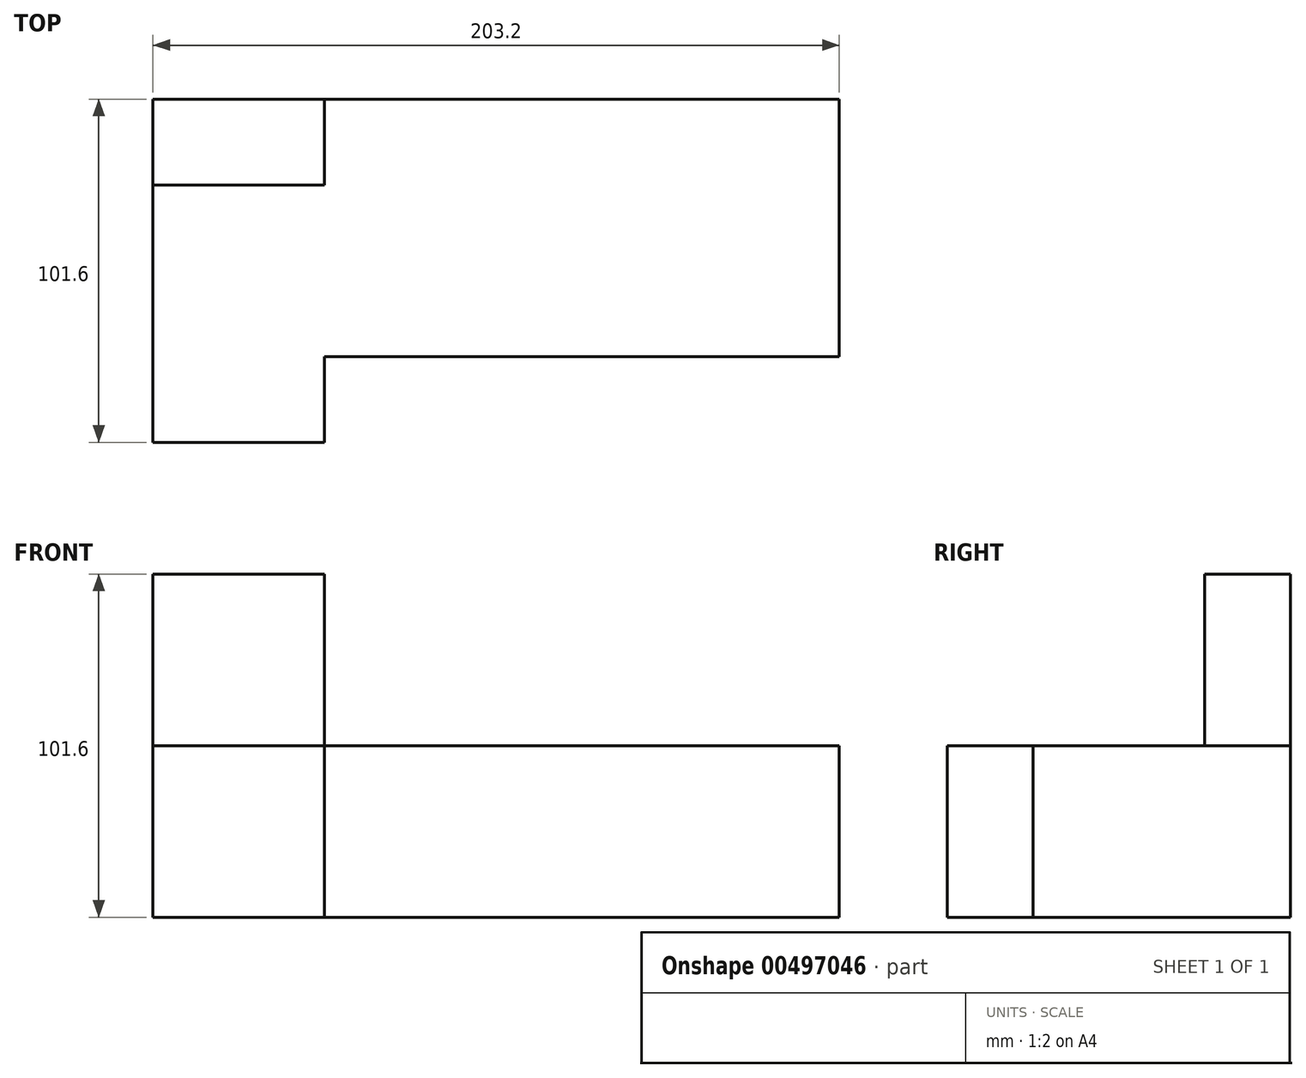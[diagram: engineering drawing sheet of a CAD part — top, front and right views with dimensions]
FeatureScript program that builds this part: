
annotation { "Feature Type Name" : "Feature", "Feature Type Description" : "" }
export const myFeature = defineFeature(function(context is Context, id is Id, definition is map)
    precondition{}
    {
        {
            var Q0;
            Q0=qCreatedBy(makeId("Front.planeOp"),FACE);
            var sketch = newSketch(context, id + "F0", { "sketchPlane" : qUnion([Q0])});
            skLineSegment(sketch, "E0.bottom", {"start": v(-73.15, 46.07) * mm, "end": v(-22.35, 46.07) * mm});
            skLineSegment(sketch, "E0.top", {"start": v(-73.15, -4.73) * mm, "end": v(-22.35, -4.73) * mm});
            skLineSegment(sketch, "E0.left", {"start": v(-73.15, 46.07) * mm, "end": v(-73.15, -4.73) * mm});
            skLineSegment(sketch, "E0.right", {"start": v(-22.35, 46.07) * mm, "end": v(-22.35, -4.73) * mm});
            skSolve(sketch);
        }
        {
            var Q0;
            Q0=makeQuery(id+"F0.imprint","IMPRINT",FACE,{"disambiguationData":[TD([[makeQuery(id+"F0.imprint","IMPRINT",EDGE,{"derivedFrom":sQuery(id+"F0.wireOp",EDGE,"E0.bottom")}),-1.0]])]});
            extrude(context, id + "F1", {"entities" : qUnion([Q0]), "depth" : 101.6 * mm});
        }
        {
            var Q0;
            Q0=makeQuery(id+"F1.opExtrude","CAP_FACE",FACE,{"disambiguationData":[OSD([sQuery(id+"F0.wireOp",EDGE,"E0.bottom"),sQuery(id+"F0.wireOp",EDGE,"E0.top"),sQuery(id+"F0.wireOp",EDGE,"E0.left"),sQuery(id+"F0.wireOp",EDGE,"E0.right")])],"isStart":true});
            var sketch = newSketch(context, id + "F2", { "sketchPlane" : qUnion([Q0])});
            skLineSegment(sketch, "E1", {"start": v(22.35, -4.73) * mm, "end": v(-130.05, -4.73) * mm});
            skLineSegment(sketch, "E2", {"start": v(-130.05, -4.73) * mm, "end": v(-130.05, 46.07) * mm});
            skLineSegment(sketch, "E3", {"start": v(-130.05, 46.07) * mm, "end": v(22.35, 46.07) * mm});
            skSolve(sketch);
        }
        {
            var Q0;
            Q0=makeQuery(id+"F2.imprint","IMPRINT",FACE,{"disambiguationData":[TD([[makeQuery(id+"F2.imprint","IMPRINT",EDGE,{"derivedFrom":sQuery(id+"F2.wireOp",EDGE,"E1")}),-1.0]])]});
            extrude(context, id + "F3", {"entities" : qUnion([Q0]), "operationType" : NewBodyOperationType.ADD, "depth" : -76.2 * mm});
        }
        {
            var Q0;
            Q0=makeQuery(id+"F3.boolean.opBoolean","MERGE",FACE,{"derivedFrom":[makeQuery(id+"F1.opExtrude","SWEPT_FACE",FACE,{"disambiguationData":[OSD([sQuery(id+"F0.wireOp",EDGE,"E0.bottom")])]}),makeQuery(id+"F3.opExtrude","SWEPT_FACE",FACE,{"disambiguationData":[OSD([sQuery(id+"F2.wireOp",EDGE,"E3")])]})]});
            var sketch = newSketch(context, id + "F4", { "sketchPlane" : qUnion([Q0])});
            skLineSegment(sketch, "E4", {"start": v(-73.15, 0) * mm, "end": v(-73.15, -25.4) * mm});
            skLineSegment(sketch, "E5", {"start": v(-73.15, 0) * mm, "end": v(-22.35, 0) * mm});
            skLineSegment(sketch, "E6", {"start": v(-22.35, 0) * mm, "end": v(-22.35, -25.4) * mm});
            skLineSegment(sketch, "E7", {"start": v(-73.15, -25.4) * mm, "end": v(-22.35, -25.4) * mm});
            skSolve(sketch);
        }
        {
            var Q0;
            Q0=makeQuery(id+"F4.imprint","IMPRINT",FACE,{"disambiguationData":[TD([[makeQuery(id+"F4.imprint","IMPRINT",EDGE,{"derivedFrom":sQuery(id+"F4.wireOp",EDGE,"E4")}),-1.0]])]});
            extrude(context, id + "F5", {"entities" : qUnion([Q0]), "operationType" : NewBodyOperationType.ADD, "depth" : 50.8 * mm});
        }
    });
